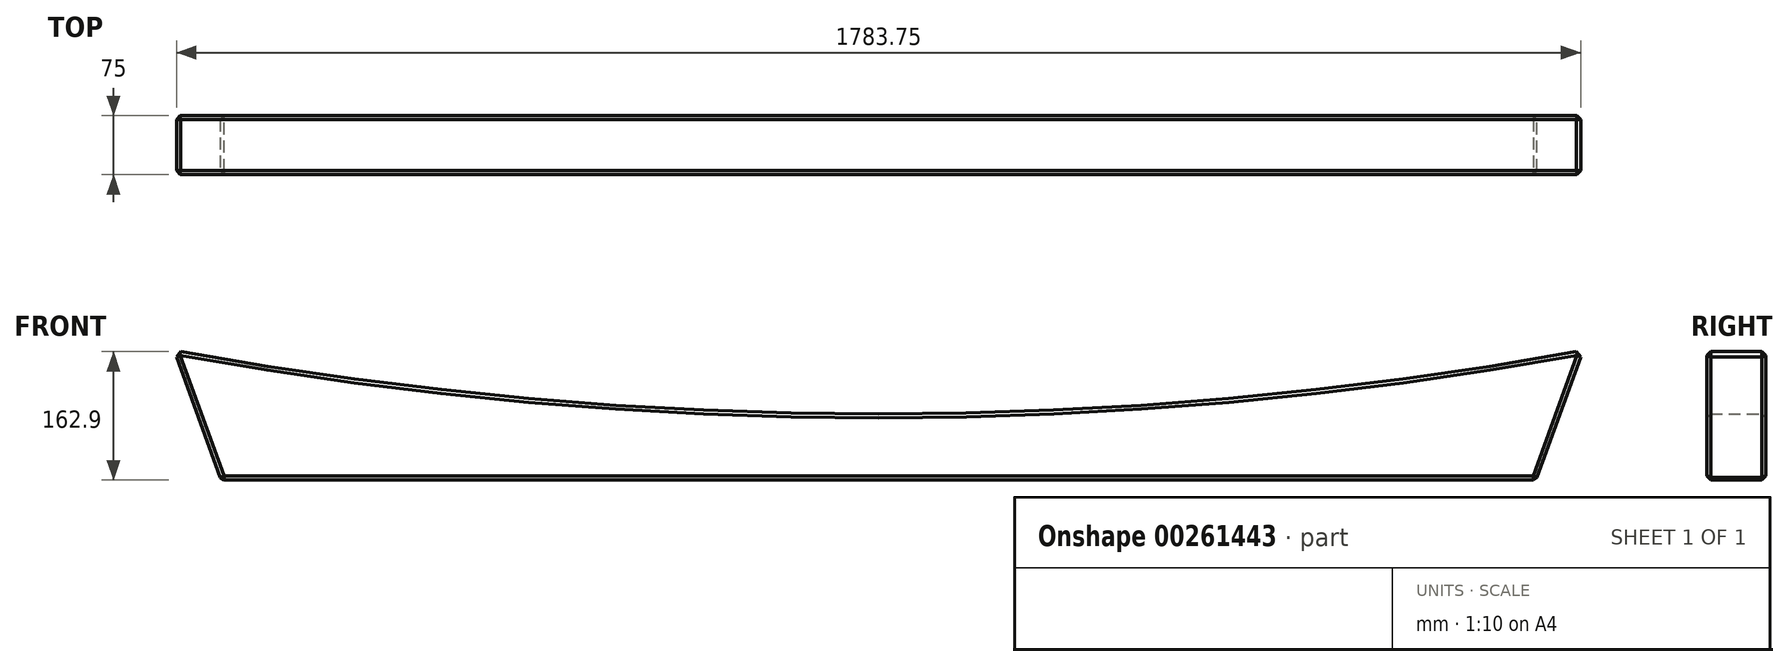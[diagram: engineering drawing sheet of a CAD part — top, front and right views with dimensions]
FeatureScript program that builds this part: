
annotation { "Feature Type Name" : "Feature", "Feature Type Description" : "" }
export const myFeature = defineFeature(function(context is Context, id is Id, definition is map)
    precondition{}
    {
        {
            var Q0;
            Q0=qCreatedBy(makeId("Front.planeOp"),FACE);
            var sketch = newSketch(context, id + "F0", { "sketchPlane" : qUnion([Q0])});
            skLineSegment(sketch, "E0", {"start": v(-64.47, 0) * mm, "end": v(1605.53, 0) * mm});
            skLineSegment(sketch, "E1", {"start": v(-64.47, 0) * mm, "end": v(-124.32, 164.45) * mm});
            skLineSegment(sketch, "E2", {"start": v(1605.53, 0) * mm, "end": v(1665.39, 164.45) * mm});
            skPoint(sketch, "E3.third.point", {"position": v(850.54, 111.3) * mm});
            skArc(sketch, "E4", {"start": v(-124.32, 164.45) * mm, "mid": v(770.53, 83.72) * mm, "end": v(1665.39, 164.45) * mm});
            skPoint(sketch, "E4.third.point", {"position": v(1010.03, 89.46) * mm});
            skSolve(sketch);
        }
        {
            var Q0;
            Q0=makeQuery(id+"F0.imprint","IMPRINT",FACE,{"disambiguationData":[TD([[makeQuery(id+"F0.imprint","IMPRINT",EDGE,{"derivedFrom":sQuery(id+"F0.wireOp",EDGE,"E0")}),1.0]])]});
            extrude(context, id + "F1", {"entities" : qUnion([Q0]), "depth" : 75 * mm});
        }
        {
            var Q0;
            Q0=makeQuery(id+"F1.opExtrude","CAP_EDGE",EDGE,{"disambiguationData":[OSD([sQuery(id+"F0.wireOp",EDGE,"E1")])],"isStart":false});
            var Q1;
            Q1=makeQuery(id+"F1.opExtrude","SWEPT_EDGE",EDGE,{"disambiguationData":[OSD([sQuery(id+"F0.wireOp",EDGE,"E0"),sQuery(id+"F0.wireOp",EDGE,"E1")])]});
            var Q2;
            Q2=makeQuery(id+"F1.opExtrude","CAP_EDGE",EDGE,{"disambiguationData":[OSD([sQuery(id+"F0.wireOp",EDGE,"E1")])],"isStart":true});
            var Q3;
            Q3=makeQuery(id+"F1.opExtrude","SWEPT_EDGE",EDGE,{"disambiguationData":[OSD([sQuery(id+"F0.wireOp",EDGE,"E1"),sQuery(id+"F0.wireOp",EDGE,"E4")])]});
            var Q4;
            Q4=makeQuery(id+"F1.opExtrude","CAP_EDGE",EDGE,{"disambiguationData":[OSD([sQuery(id+"F0.wireOp",EDGE,"E0")])],"isStart":false});
            var Q5;
            Q5=makeQuery(id+"F1.opExtrude","CAP_EDGE",EDGE,{"disambiguationData":[OSD([sQuery(id+"F0.wireOp",EDGE,"E0")])],"isStart":true});
            var Q6;
            Q6=makeQuery(id+"F1.opExtrude","CAP_EDGE",EDGE,{"disambiguationData":[OSD([sQuery(id+"F0.wireOp",EDGE,"E4")])],"isStart":false});
            var Q7;
            Q7=makeQuery(id+"F1.opExtrude","CAP_EDGE",EDGE,{"disambiguationData":[OSD([sQuery(id+"F0.wireOp",EDGE,"E4")])],"isStart":true});
            var Q8;
            Q8=makeQuery(id+"F1.opExtrude","CAP_EDGE",EDGE,{"disambiguationData":[OSD([sQuery(id+"F0.wireOp",EDGE,"E2")])],"isStart":false});
            var Q9;
            Q9=makeQuery(id+"F1.opExtrude","SWEPT_EDGE",EDGE,{"disambiguationData":[OSD([sQuery(id+"F0.wireOp",EDGE,"E0"),sQuery(id+"F0.wireOp",EDGE,"E2")])]});
            var Q10;
            Q10=makeQuery(id+"F1.opExtrude","CAP_EDGE",EDGE,{"disambiguationData":[OSD([sQuery(id+"F0.wireOp",EDGE,"E2")])],"isStart":true});
            var Q11;
            Q11=makeQuery(id+"F1.opExtrude","SWEPT_EDGE",EDGE,{"disambiguationData":[OSD([sQuery(id+"F0.wireOp",EDGE,"E2"),sQuery(id+"F0.wireOp",EDGE,"E4")])]});
            chamfer(context, id + "F2", {"entities" : qUnion([Q0, Q1, Q2, Q3, Q4, Q5, Q6, Q7, Q8, Q9, Q10, Q11]), "width" : 5 * mm, "tangentPropagation" : true});
        }
    });
